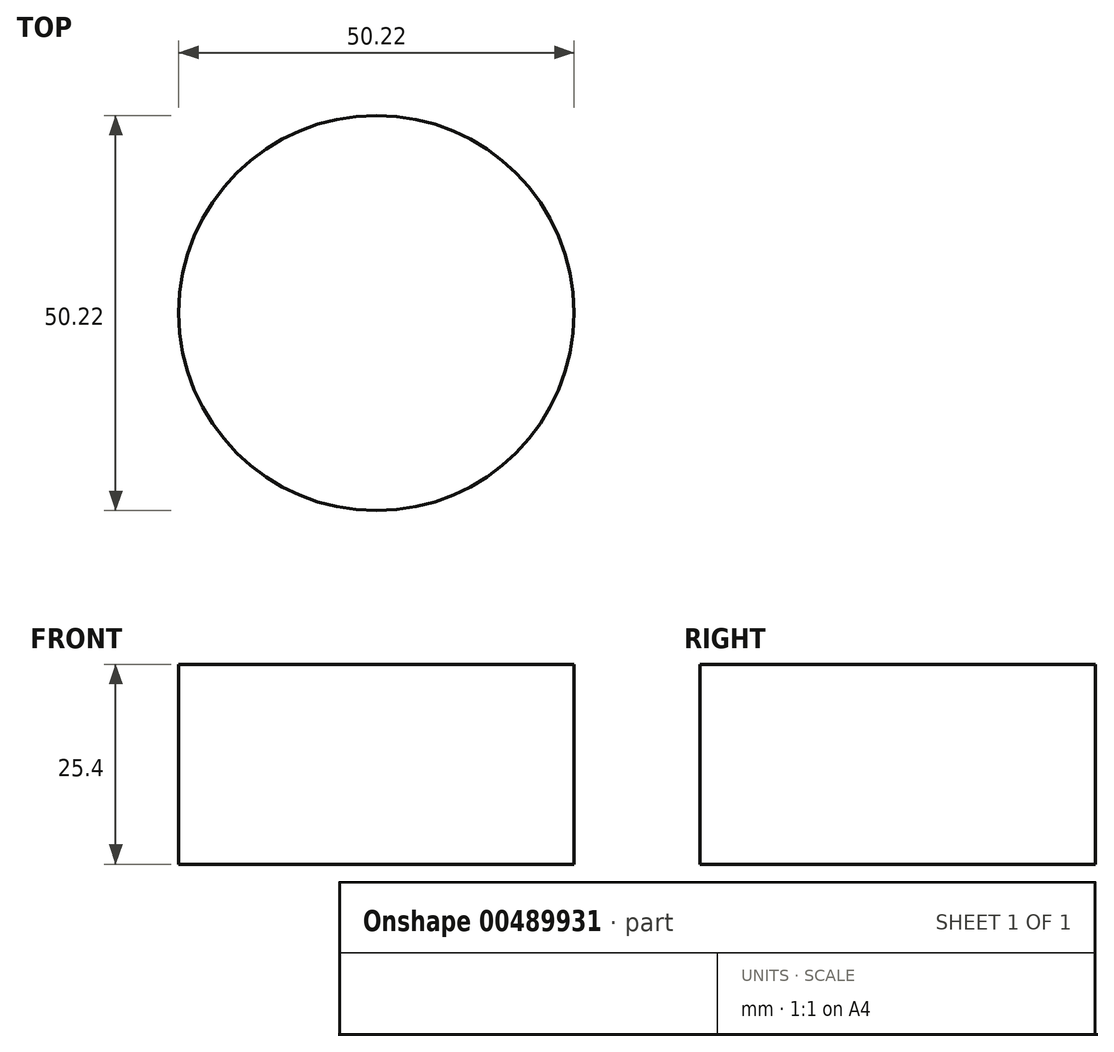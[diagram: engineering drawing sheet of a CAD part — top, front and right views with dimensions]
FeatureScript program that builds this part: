
annotation { "Feature Type Name" : "Feature", "Feature Type Description" : "" }
export const myFeature = defineFeature(function(context is Context, id is Id, definition is map)
    precondition{}
    {
        {
            var Q0;
            Q0=qCreatedBy(makeId("Top.planeOp"),FACE);
            var sketch = newSketch(context, id + "F0", { "sketchPlane" : qUnion([Q0])});
            skCircle(sketch, "E0", {"center": v(3.05, -1.9) * mm, "radius": 25.1 * mm});
            skSolve(sketch);
        }
        {
            var Q0;
            Q0 = qSketchRegion(id + "F0", true);
            extrude(context, id + "F1", {"entities" : qUnion([Q0]), "depth" : 25.4 * mm});
        }
        {
            var Q0;
            Q0=qCreatedBy(makeId("Front.planeOp"),FACE);
            var sketch = newSketch(context, id + "F2", { "sketchPlane" : qUnion([Q0])});
            skCircle(sketch, "E1", {"center": v(2.83, 13.14) * mm, "radius": 3.62 * mm});
            skSolve(sketch);
        }
        {
            var Q0;
            Q0=sQuery(id+"F2.wireOp",EDGE,"E1");
            extrude(context, id + "F3", {"bodyType" : ToolBodyType.SURFACE, "surfaceEntities" : qUnion([Q0]), "depth" : 76.2 * mm});
        }
    });
